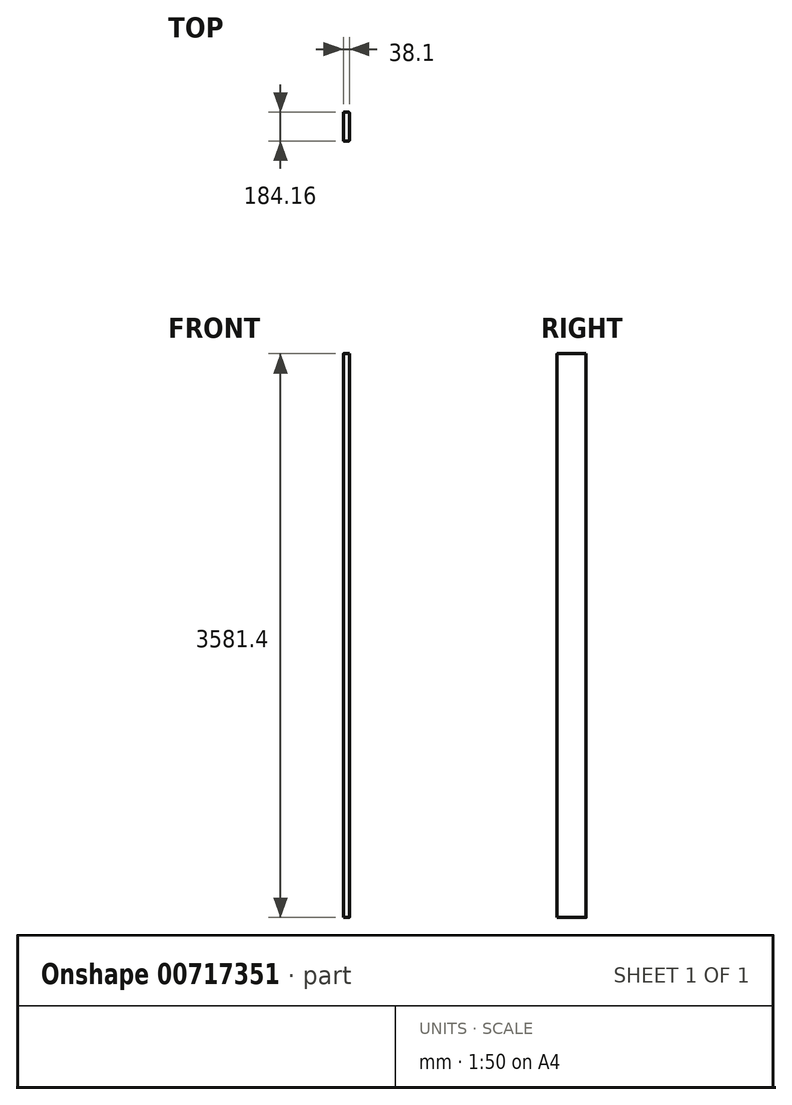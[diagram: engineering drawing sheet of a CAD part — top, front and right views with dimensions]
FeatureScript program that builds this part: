
annotation { "Feature Type Name" : "Feature", "Feature Type Description" : "" }
export const myFeature = defineFeature(function(context is Context, id is Id, definition is map)
    precondition{}
    {
        {
            var Q0;
            Q0=qCreatedBy(makeId("Top.planeOp"),FACE);
            var sketch = newSketch(context, id + "F0", { "sketchPlane" : qUnion([Q0])});
            skLineSegment(sketch, "E0.bottom", {"start": v(-12.7, 92.08) * mm, "end": v(12.7, 92.08) * mm});
            skLineSegment(sketch, "E0.top", {"start": v(-12.7, -92.08) * mm, "end": v(12.7, -92.08) * mm});
            skLineSegment(sketch, "E0.left", {"start": v(-19.05, 85.73) * mm, "end": v(-19.05, -85.73) * mm});
            skLineSegment(sketch, "E0.right", {"start": v(19.05, 85.73) * mm, "end": v(19.05, -85.73) * mm});
            skLineSegment(sketch, "E1", {"start": v(-19.05, -92.08) * mm, "end": v(19.05, 92.08) * mm, "construction": true});
            skPoint(sketch, "E2.visualSharp", {"position": v(19.05, 92.08) * mm});
            skArc(sketch, "E2.filletArc", {"start": v(19.05, 85.73) * mm, "mid": v(17.2, 90.22) * mm, "end": v(12.7, 92.08) * mm});
            skPoint(sketch, "E3.visualSharp", {"position": v(-19.05, 92.08) * mm});
            skArc(sketch, "E3.filletArc", {"start": v(-12.7, 92.08) * mm, "mid": v(-17.2, 90.22) * mm, "end": v(-19.05, 85.73) * mm});
            skPoint(sketch, "E4.visualSharp", {"position": v(-19.05, -92.08) * mm});
            skArc(sketch, "E4.filletArc", {"start": v(-19.05, -85.73) * mm, "mid": v(-17.2, -90.22) * mm, "end": v(-12.7, -92.08) * mm});
            skPoint(sketch, "E5.visualSharp", {"position": v(19.05, -92.08) * mm});
            skArc(sketch, "E5.filletArc", {"start": v(12.7, -92.08) * mm, "mid": v(17.2, -90.22) * mm, "end": v(19.05, -85.73) * mm});
            skSolve(sketch);
        }
        {
            var Q0;
            Q0=makeQuery(id+"F0.imprint","IMPRINT",FACE,{"disambiguationData":[TD([[makeQuery(id+"F0.imprint","IMPRINT",EDGE,{"derivedFrom":sQuery(id+"F0.wireOp",EDGE,"E0.bottom")}),-1.0]])]});
            extrude(context, id + "F1", {"entities" : qUnion([Q0]), "depth" : 3581.4 * mm, "offsetDistance" : 25.4 * mm});
        }
    });
